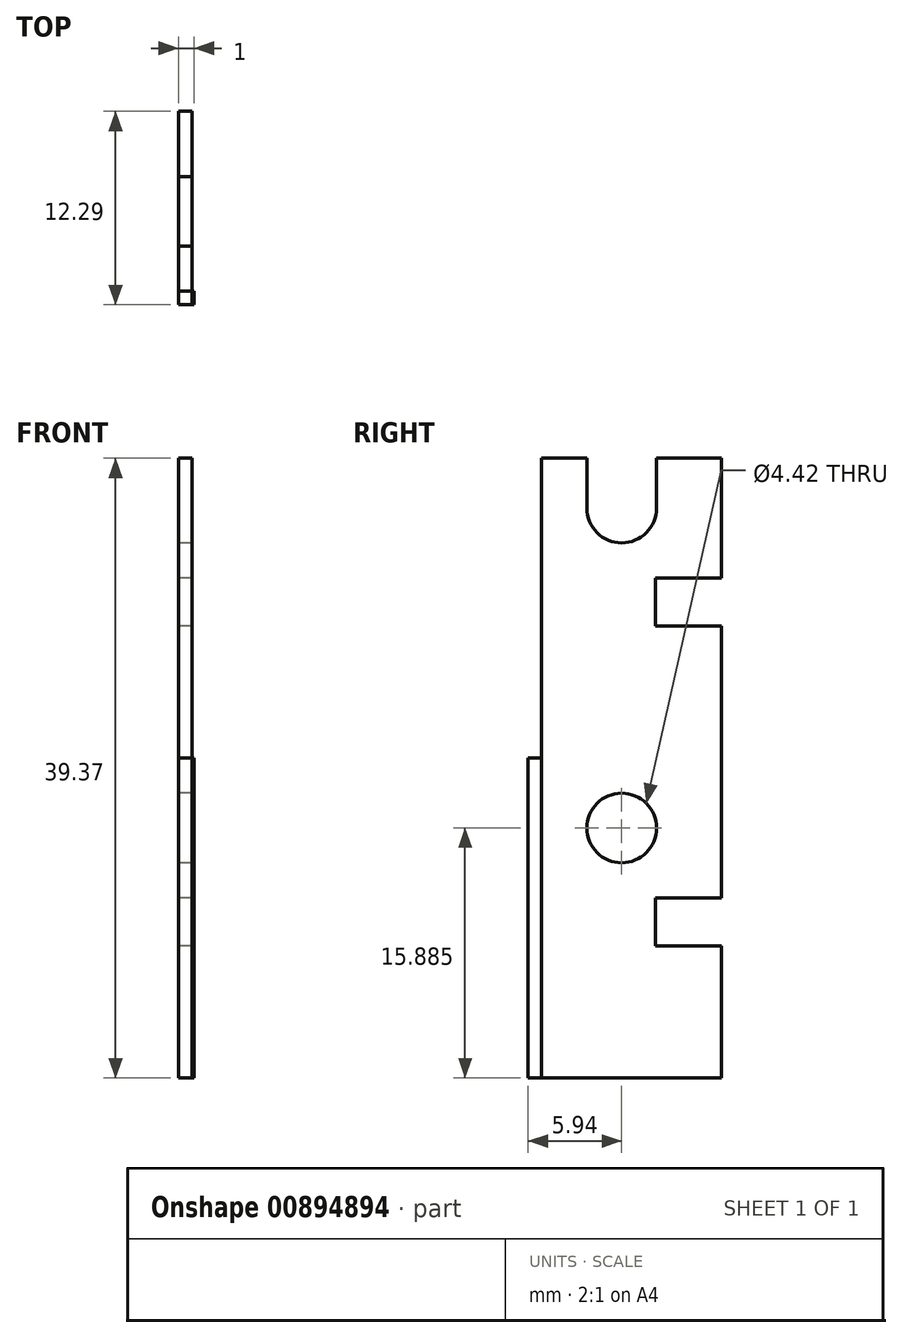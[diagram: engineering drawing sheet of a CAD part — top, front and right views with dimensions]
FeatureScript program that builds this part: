
annotation { "Feature Type Name" : "Feature", "Feature Type Description" : "" }
export const myFeature = defineFeature(function(context is Context, id is Id, definition is map)
    precondition{}
    {
        {
            var Q0;
            Q0=qCreatedBy(makeId("Top.planeOp"),FACE);
            var sketch = newSketch(context, id + "F0", { "sketchPlane" : qUnion([Q0])});
            skLineSegment(sketch, "E0.bottom", {"start": v(-137.4, -240.84) * mm, "end": v(-114.55, -240.84) * mm});
            skLineSegment(sketch, "E0.top", {"start": v(-137.4, 57.16) * mm, "end": v(-114.55, 57.16) * mm});
            skLineSegment(sketch, "E0.left", {"start": v(-137.4, -240.84) * mm, "end": v(-137.4, 57.16) * mm});
            skLineSegment(sketch, "E0.right", {"start": v(-114.55, -240.84) * mm, "end": v(-114.55, 57.16) * mm});
            skPoint(sketch, "E1", {"position": v(-3.4, -240.84) * mm});
            skLineSegment(sketch, "E2", {"start": v(11.76, 58.2) * mm, "end": v(11.76, 59.05) * mm});
            skLineSegment(sketch, "E3", {"start": v(11.76, 59.05) * mm, "end": v(-108.26, 59.05) * mm});
            skLineSegment(sketch, "E4", {"start": v(-108.26, 59.05) * mm, "end": v(-108.26, 70.48) * mm});
            skLineSegment(sketch, "E5", {"start": v(-108.26, 70.48) * mm, "end": v(-109.12, 70.48) * mm});
            skLineSegment(sketch, "E6.bottom", {"start": v(-114.55, -240.84) * mm, "end": v(-16.15, -240.84) * mm});
            skLineSegment(sketch, "E6.top", {"start": v(-114.55, 57.16) * mm, "end": v(-16.15, 57.16) * mm});
            skLineSegment(sketch, "E6.right", {"start": v(-16.15, -240.84) * mm, "end": v(-16.15, 57.16) * mm});
            skLineSegment(sketch, "E7.bottom", {"start": v(-16.15, 57.16) * mm, "end": v(-7.9, 57.16) * mm});
            skLineSegment(sketch, "E7.top", {"start": v(-16.15, 42.16) * mm, "end": v(-7.9, 42.16) * mm});
            skLineSegment(sketch, "E7.left", {"start": v(-16.15, 57.16) * mm, "end": v(-16.15, 42.16) * mm});
            skLineSegment(sketch, "E7.right", {"start": v(-7.9, 57.16) * mm, "end": v(-7.9, 42.16) * mm});
            skPoint(sketch, "E8", {"position": v(-7.9, -240.84) * mm});
            skLineSegment(sketch, "E9.bottom", {"start": v(-16.15, 23.8) * mm, "end": v(-7.9, 23.8) * mm});
            skLineSegment(sketch, "E9.top", {"start": v(-16.15, 15.8) * mm, "end": v(-7.9, 15.8) * mm});
            skLineSegment(sketch, "E9.left", {"start": v(-16.15, 23.8) * mm, "end": v(-16.15, 15.8) * mm});
            skLineSegment(sketch, "E9.right", {"start": v(-7.9, 23.8) * mm, "end": v(-7.9, 15.8) * mm});
            skPoint(sketch, "E10", {"position": v(-3.4, 57.16) * mm});
            skLineSegment(sketch, "E11", {"start": v(-16.15, 12.15) * mm, "end": v(-3.4, 12.15) * mm});
            skLineSegment(sketch, "E12", {"start": v(-3.4, 12.15) * mm, "end": v(-3.4, 0.95) * mm});
            skLineSegment(sketch, "E13", {"start": v(-3.4, 0.95) * mm, "end": v(-11.8, 0.95) * mm});
            skLineSegment(sketch, "E14", {"start": v(-11.8, 0.95) * mm, "end": v(-11.8, -0.95) * mm});
            skLineSegment(sketch, "E15", {"start": v(-11.8, -0.95) * mm, "end": v(-3.4, -0.95) * mm});
            skLineSegment(sketch, "E16", {"start": v(-3.4, -0.95) * mm, "end": v(-3.4, -72.15) * mm});
            skLineSegment(sketch, "E17", {"start": v(-3.4, -72.15) * mm, "end": v(-16.15, -72.15) * mm});
            skPoint(sketch, "E18", {"position": v(-11.8, 0) * mm});
            skArc(sketch, "E19", {"start": v(-14.32, 15.8) * mm, "mid": v(-16.15, 13.98) * mm, "end": v(-14.32, 12.15) * mm});
            skArc(sketch, "E20", {"start": v(-10.85, 0.95) * mm, "mid": v(-11.8, 0) * mm, "end": v(-10.85, -0.95) * mm});
            skLineSegment(sketch, "E21", {"start": v(-16.15, -81.9) * mm, "end": v(-11.35, -81.9) * mm});
            skLineSegment(sketch, "E22", {"start": v(-11.35, -81.9) * mm, "end": v(-11.35, -87.6) * mm});
            skLineSegment(sketch, "E23", {"start": v(-11.35, -87.6) * mm, "end": v(-8.77, -87.6) * mm});
            skLineSegment(sketch, "E24", {"start": v(-8.77, -87.6) * mm, "end": v(-6.35, -86.2) * mm});
            skLineSegment(sketch, "E25", {"start": v(-6.35, -86.2) * mm, "end": v(-6.35, -74.9) * mm});
            skLineSegment(sketch, "E26", {"start": v(-6.35, -74.9) * mm, "end": v(-12.38, -74.9) * mm});
            skLineSegment(sketch, "E27", {"start": v(-12.38, -74.9) * mm, "end": v(-12.38, -72.15) * mm});
            skArc(sketch, "E28", {"start": v(-11, -72.15) * mm, "mid": v(-12.38, -73.53) * mm, "end": v(-11, -74.9) * mm});
            skLineSegment(sketch, "E29", {"start": v(-108.26, 59.05) * mm, "end": v(-109.12, 59.05) * mm});
            skLineSegment(sketch, "E30", {"start": v(-109.12, 70.48) * mm, "end": v(-109.12, 59.05) * mm});
            skLineSegment(sketch, "E31", {"start": v(-109.12, 58.2) * mm, "end": v(-109.12, 59.05) * mm});
            skLineSegment(sketch, "E32", {"start": v(-108.26, 59.05) * mm, "end": v(-108.26, 58.2) * mm});
            skLineSegment(sketch, "E33", {"start": v(-108.26, 58.2) * mm, "end": v(-109.12, 58.2) * mm});
            skLineSegment(sketch, "E34", {"start": v(-108.26, 58.2) * mm, "end": v(11.76, 58.2) * mm});
            skPoint(sketch, "E35", {"position": v(0, 0) * mm});
            skPoint(sketch, "E36", {"position": v(0, 57.16) * mm});
            skSolve(sketch);
        }
        {
            var Q0;
            Q0=makeQuery(id+"F0.imprint","IMPRINT",FACE,{"disambiguationData":[TD([[makeQuery(id+"F0.imprint","IMPRINT",EDGE,{"derivedFrom":sQuery(id+"F0.wireOp",EDGE,"E2")}),1.0]])]});
            extrude(context, id + "F1", {"entities" : qUnion([Q0]), "depth" : 10 * mm, "hasSecondDirection" : true, "secondDirectionOppositeDirection" : true, "secondDirectionDepth" : 40 * mm});
        }
        {
            var Q0;
            Q0=makeQuery(id+"F1.opExtrude","SWEPT_FACE",FACE,{"disambiguationData":[OSD([sQuery(id+"F0.wireOp",EDGE,"E3")])]});
            var sketch = newSketch(context, id + "F2", { "sketchPlane" : qUnion([Q0])});
            skLineSegment(sketch, "E37", {"start": v(-4.49, -2.06) * mm, "end": v(-11.76, -2.06) * mm});
            skLineSegment(sketch, "E38", {"start": v(-11.76, -2.06) * mm, "end": v(-11.76, -12.25) * mm});
            skLineSegment(sketch, "E39", {"start": v(-11.76, -12.25) * mm, "end": v(-4.49, -12.25) * mm});
            skLineSegment(sketch, "E40", {"start": v(-4.49, -12.25) * mm, "end": v(-0.38, -16.37) * mm});
            skLineSegment(sketch, "E41", {"start": v(-0.38, -16.36) * mm, "end": v(101.78, -16.36) * mm});
            skLineSegment(sketch, "E42", {"start": v(108.26, -13.82) * mm, "end": v(108.26, 5.23) * mm});
            skLineSegment(sketch, "E43", {"start": v(108.26, 5.23) * mm, "end": v(105.34, 5.23) * mm});
            skLineSegment(sketch, "E44", {"start": v(103.7, 2.06) * mm, "end": v(-0.37, 2.05) * mm});
            skLineSegment(sketch, "E45", {"start": v(-0.37, 2.05) * mm, "end": v(-4.49, -2.06) * mm});
            skLineSegment(sketch, "E46.bottom", {"start": v(7.9, 0.79) * mm, "end": v(114.55, 0.79) * mm});
            skLineSegment(sketch, "E46.top", {"start": v(7.9, -0.78) * mm, "end": v(114.55, -0.78) * mm});
            skLineSegment(sketch, "E46.left", {"start": v(7.9, 0.78) * mm, "end": v(7.9, -0.78) * mm});
            skLineSegment(sketch, "E46.right", {"start": v(114.55, 0.79) * mm, "end": v(114.55, -0.78) * mm});
            skPoint(sketch, "E47", {"position": v(7.9, 0) * mm});
            skLineSegment(sketch, "E48", {"start": v(108.26, -13.82) * mm, "end": v(104.32, -13.82) * mm});
            skLineSegment(sketch, "E49", {"start": v(104.32, -13.82) * mm, "end": v(101.78, -16.36) * mm});
            skLineSegment(sketch, "E50", {"start": v(103.7, 2.05) * mm, "end": v(103.7, 3.59) * mm});
            skLineSegment(sketch, "E51", {"start": v(103.7, 3.59) * mm, "end": v(105.34, 5.23) * mm});
            skPoint(sketch, "E52", {"position": v(0, 0) * mm});
            skLineSegment(sketch, "E53", {"start": v(-11.76, -22.39) * mm, "end": v(-11.76, -32.58) * mm});
            skLineSegment(sketch, "E54", {"start": v(-11.76, -32.57) * mm, "end": v(-4.49, -32.57) * mm});
            skLineSegment(sketch, "E55", {"start": v(-4.49, -32.57) * mm, "end": v(-0.38, -36.69) * mm});
            skLineSegment(sketch, "E56", {"start": v(-0.38, -36.69) * mm, "end": v(101.78, -36.68) * mm});
            skLineSegment(sketch, "E57", {"start": v(104.32, -34.14) * mm, "end": v(101.78, -36.68) * mm});
            skLineSegment(sketch, "E58", {"start": v(104.32, -34.14) * mm, "end": v(108.26, -34.14) * mm});
            skLineSegment(sketch, "E59", {"start": v(108.26, -34.14) * mm, "end": v(108.26, -15.1) * mm});
            skLineSegment(sketch, "E60", {"start": v(108.26, -15.1) * mm, "end": v(105.34, -15.1) * mm});
            skLineSegment(sketch, "E61", {"start": v(105.34, -15.1) * mm, "end": v(103.7, -16.73) * mm});
            skLineSegment(sketch, "E62", {"start": v(103.7, -16.73) * mm, "end": v(103.7, -18.26) * mm});
            skLineSegment(sketch, "E63", {"start": v(103.7, -18.26) * mm, "end": v(-0.37, -18.27) * mm});
            skLineSegment(sketch, "E64", {"start": v(-11.76, -22.39) * mm, "end": v(-4.49, -22.39) * mm});
            skLineSegment(sketch, "E65", {"start": v(-4.49, -22.39) * mm, "end": v(-0.37, -18.27) * mm});
            skLineSegment(sketch, "E66", {"start": v(-0.38, -16.37) * mm, "end": v(-0.37, -18.27) * mm});
            skLineSegment(sketch, "E67", {"start": v(108.26, -13.82) * mm, "end": v(108.26, -15.1) * mm});
            skSolve(sketch);
        }
        {
            var Q0;
            Q0=qSketchRegion(id+"F2",true);
            extrude(context, id + "F3", {"entities" : qUnion([Q0]), "operationType" : NewBodyOperationType.INTERSECT, "oppositeDirection" : true, "depth" : 5 * mm});
        }
        {
            var Q0;
            Q0=makeQuery(id+"F0.imprint","IMPRINT",FACE,{"disambiguationData":[TD([[makeQuery(id+"F0.imprint","IMPRINT",EDGE,{"derivedFrom":sQuery(id+"F0.wireOp",EDGE,"E29")}),1.0]])]});
            var Q1;
            Q1=makeQuery(id+"F0.imprint","IMPRINT",FACE,{"disambiguationData":[TD([[makeQuery(id+"F0.imprint","IMPRINT",EDGE,{"derivedFrom":sQuery(id+"F0.wireOp",EDGE,"E4")}),1.0]])]});
            extrude(context, id + "F4", {"entities" : qUnion([Q0, Q1]), "depth" : 10 * mm, "hasSecondDirection" : true, "secondDirectionOppositeDirection" : true, "secondDirectionDepth" : 40 * mm});
        }
        {
            var Q0;
            Q0=makeQuery(id+"F4.opExtrude","SWEPT_FACE",FACE,{"disambiguationData":[OSD([sQuery(id+"F0.wireOp",EDGE,"E30"),sQuery(id+"F0.wireOp",EDGE,"E31")])]});
            var sketch = newSketch(context, id + "F5", { "sketchPlane" : qUnion([Q0])});
            skLineSegment(sketch, "E68", {"start": v(-70.48, 5.23) * mm, "end": v(-70.48, -2.4) * mm});
            skLineSegment(sketch, "E69", {"start": v(-70.48, -2.4) * mm, "end": v(-66.29, -2.4) * mm});
            skLineSegment(sketch, "E70", {"start": v(-66.3, -2.4) * mm, "end": v(-66.3, -5.44) * mm});
            skLineSegment(sketch, "E71", {"start": v(-66.3, -5.44) * mm, "end": v(-70.48, -5.44) * mm});
            skLineSegment(sketch, "E72", {"start": v(-70.48, -5.44) * mm, "end": v(-70.48, -13.83) * mm});
            skLineSegment(sketch, "E73", {"start": v(-58.19, -13.83) * mm, "end": v(-58.19, 5.22) * mm});
            skLineSegment(sketch, "E74", {"start": v(-61.92, 5.22) * mm, "end": v(-61.92, -0.16) * mm});
            skLineSegment(sketch, "E75", {"start": v(-61.92, -0.15) * mm, "end": v(-66.34, -0.16) * mm});
            skLineSegment(sketch, "E76", {"start": v(-66.34, -0.16) * mm, "end": v(-66.34, 5.23) * mm});
            skLineSegment(sketch, "E77", {"start": v(-66.34, 5.23) * mm, "end": v(-70.48, 5.23) * mm});
            skPoint(sketch, "E78", {"position": v(-70.48, -16.37) * mm});
            skArc(sketch, "E79", {"start": v(-66.34, 2.06) * mm, "mid": v(-64.13, -0.16) * mm, "end": v(-61.92, 2.06) * mm});
            skLineSegment(sketch, "E80.bottom", {"start": v(-57.16, 0.79) * mm, "end": v(0, 0.79) * mm});
            skLineSegment(sketch, "E80.top", {"start": v(-57.16, -0.79) * mm, "end": v(0, -0.79) * mm});
            skLineSegment(sketch, "E80.left", {"start": v(-57.16, 0.79) * mm, "end": v(-57.16, -0.79) * mm});
            skPoint(sketch, "E81", {"position": v(-57.16, 0) * mm});
            skLineSegment(sketch, "E82.bottom", {"start": v(-46.48, 1.65) * mm, "end": v(-58.19, 1.65) * mm});
            skLineSegment(sketch, "E82.top", {"start": v(-46.48, 0.78) * mm, "end": v(-58.19, 0.78) * mm});
            skLineSegment(sketch, "E82.left", {"start": v(-46.48, 1.65) * mm, "end": v(-46.48, 0.78) * mm});
            skLineSegment(sketch, "E82.right", {"start": v(-58.19, 1.65) * mm, "end": v(-58.19, 0.78) * mm});
            skLineSegment(sketch, "E83", {"start": v(-59.05, 5.22) * mm, "end": v(-59.05, -13.83) * mm});
            skLineSegment(sketch, "E84", {"start": v(-61.92, 5.22) * mm, "end": v(-59.05, 5.22) * mm});
            skLineSegment(sketch, "E85", {"start": v(-59.05, 5.22) * mm, "end": v(-58.19, 5.22) * mm});
            skPoint(sketch, "E86", {"position": v(0, 0) * mm});
            skLineSegment(sketch, "E87", {"start": v(-59.05, -15.1) * mm, "end": v(-70.48, -15.1) * mm});
            skLineSegment(sketch, "E88", {"start": v(-70.48, -15.1) * mm, "end": v(-70.48, -22.71) * mm});
            skLineSegment(sketch, "E89", {"start": v(-70.48, -22.71) * mm, "end": v(-66.3, -22.71) * mm});
            skLineSegment(sketch, "E90", {"start": v(-66.3, -22.71) * mm, "end": v(-66.3, -25.76) * mm});
            skLineSegment(sketch, "E91", {"start": v(-66.3, -25.76) * mm, "end": v(-70.48, -25.76) * mm});
            skLineSegment(sketch, "E92", {"start": v(-70.48, -25.76) * mm, "end": v(-70.48, -34.14) * mm});
            skLineSegment(sketch, "E93", {"start": v(-70.48, -34.14) * mm, "end": v(-59.05, -34.14) * mm});
            skLineSegment(sketch, "E94", {"start": v(-59.05, -34.14) * mm, "end": v(-59.05, -15.1) * mm});
            skLineSegment(sketch, "E95.bottom", {"start": v(-59.05, -15.1) * mm, "end": v(-58.19, -15.1) * mm});
            skLineSegment(sketch, "E95.top", {"start": v(-59.05, -34.14) * mm, "end": v(-58.19, -34.14) * mm});
            skLineSegment(sketch, "E95.left", {"start": v(-59.05, -15.1) * mm, "end": v(-59.05, -34.14) * mm});
            skLineSegment(sketch, "E95.right", {"start": v(-58.19, -15.1) * mm, "end": v(-58.19, -34.14) * mm});
            skLineSegment(sketch, "E96", {"start": v(-59.05, -13.83) * mm, "end": v(-70.48, -13.83) * mm});
            skLineSegment(sketch, "E97", {"start": v(-59.05, -13.83) * mm, "end": v(-58.19, -13.83) * mm});
            skLineSegment(sketch, "E98.bottom", {"start": v(-70.48, -13.83) * mm, "end": v(-58.19, -13.83) * mm});
            skLineSegment(sketch, "E98.top", {"start": v(-70.48, -15.1) * mm, "end": v(-58.19, -15.1) * mm});
            skLineSegment(sketch, "E98.left", {"start": v(-70.48, -13.83) * mm, "end": v(-70.48, -15.1) * mm});
            skLineSegment(sketch, "E98.right", {"start": v(-58.19, -13.83) * mm, "end": v(-58.19, -15.1) * mm});
            skCircle(sketch, "E99", {"center": v(-64.13, -18.27) * mm, "radius": 2.2 * mm});
            skSolve(sketch);
        }
        {
            var Q0;
            {var subQ0=sQuery(id+"F5.wireOp",EDGE,"E76");var subQ1=sQuery(id+"F5.wireOp",EDGE,"E75");var subQ2=makeQuery(id+"F5.imprint","INTERSECT",VERTEX,{"derivedFrom":[subQ1,subQ0]});Q0=makeQuery(id+"F5.imprint","IMPRINT",FACE,{"disambiguationData":[TD([[makeQuery(id+"F5.imprint","IMPRINT",EDGE,{"disambiguationData":[TD([[subQ2,1.0]])],"derivedFrom":subQ1}),-1.0]])]});}
            var Q1;
            Q1=makeQuery(id+"F5.imprint","IMPRINT",FACE,{"disambiguationData":[TD([[makeQuery(id+"F5.imprint","IMPRINT",EDGE,{"derivedFrom":sQuery(id+"F5.wireOp",EDGE,"E68")}),1.0]])]});
            var Q2;
            {var subQ0=sQuery(id+"F5.wireOp",EDGE,"E75");var subQ1=sQuery(id+"F5.wireOp",EDGE,"E74");var subQ2=makeQuery(id+"F5.imprint","INTERSECT",VERTEX,{"derivedFrom":[subQ1,subQ0]});Q2=makeQuery(id+"F5.imprint","IMPRINT",FACE,{"disambiguationData":[TD([[makeQuery(id+"F5.imprint","IMPRINT",EDGE,{"disambiguationData":[TD([[subQ2,1.0]])],"derivedFrom":subQ1}),-1.0]])]});}
            var Q3;
            {var subQ3=sQuery(id+"F5.wireOp",EDGE,"E82.right");Q3=makeQuery(id+"F5.imprint","IMPRINT",FACE,{"disambiguationData":[TD([[makeQuery(id+"F5.imprint","IMPRINT",EDGE,{"derivedFrom":subQ3}),-1.0]])]});}
            var Q4;
            {var subQ0=sQuery(id+"F5.wireOp",EDGE,"E98.left");Q4=makeQuery(id+"F5.imprint","IMPRINT",FACE,{"disambiguationData":[TD([[makeQuery(id+"F5.imprint","IMPRINT",EDGE,{"derivedFrom":subQ0}),1.0]])]});}
            var Q5;
            {var subQ0=sQuery(id+"F5.wireOp",EDGE,"E88");Q5=makeQuery(id+"F5.imprint","IMPRINT",FACE,{"disambiguationData":[TD([[makeQuery(id+"F5.imprint","IMPRINT",EDGE,{"derivedFrom":subQ0}),1.0]])]});}
            var Q6;
            Q6=makeQuery(id+"F5.imprint","IMPRINT",FACE,{"disambiguationData":[TD([[makeQuery(id+"F5.imprint","IMPRINT",EDGE,{"derivedFrom":sQuery(id+"F5.wireOp",EDGE,"E95.top")}),1.0]])]});
            extrude(context, id + "F6", {"entities" : qUnion([Q0, Q1, Q2, Q3, Q4, Q5, Q6]), "operationType" : NewBodyOperationType.INTERSECT, "oppositeDirection" : true, "depth" : 1 * mm});
        }
    });
